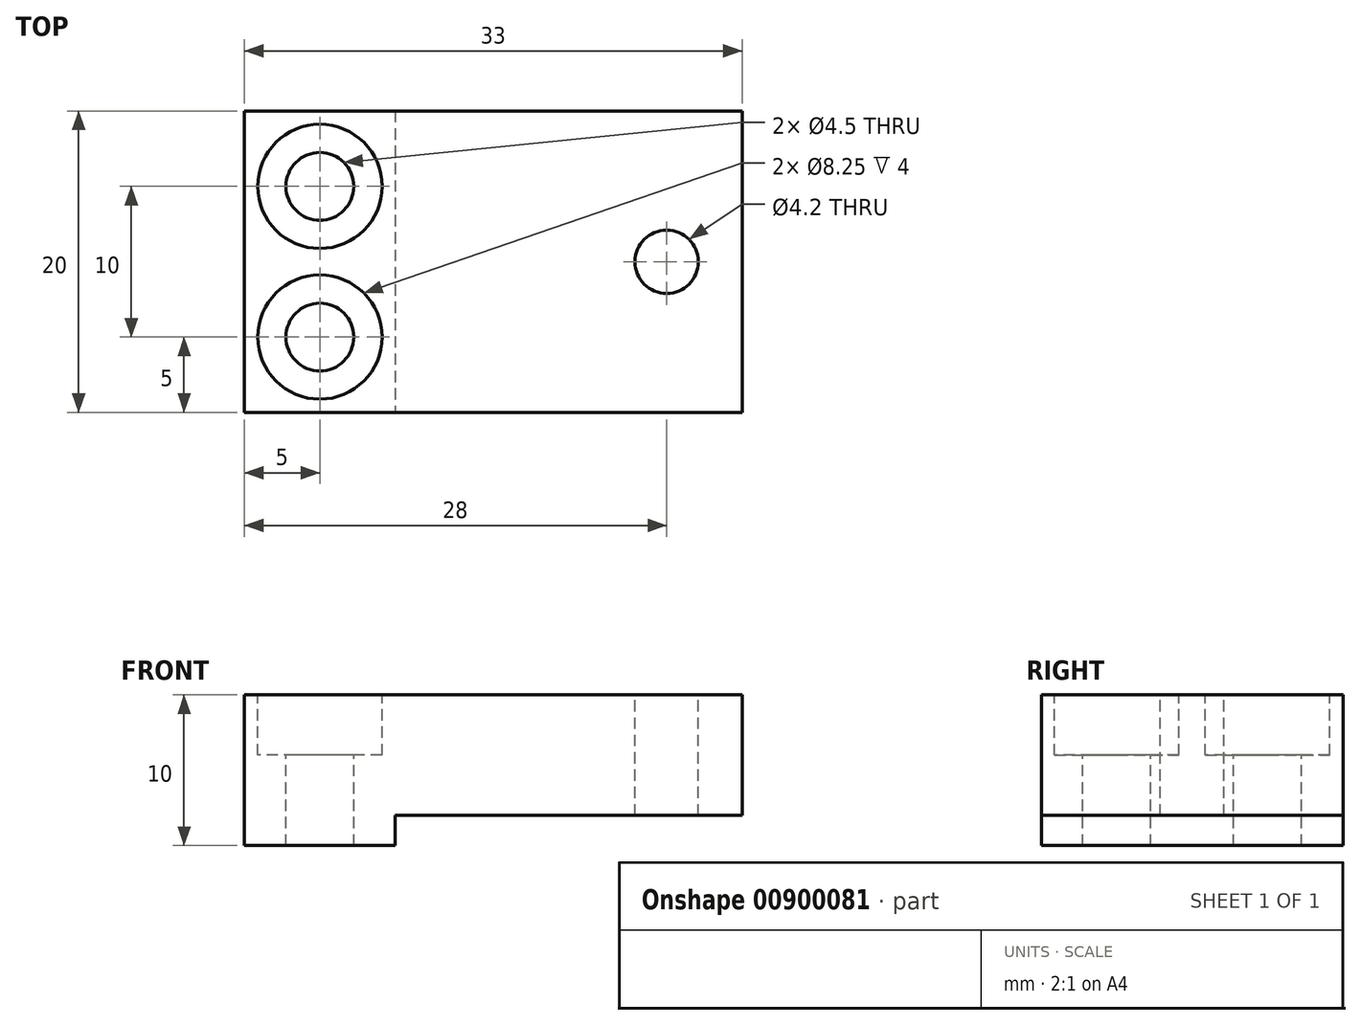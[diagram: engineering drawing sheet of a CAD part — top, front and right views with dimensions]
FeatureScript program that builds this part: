
annotation { "Feature Type Name" : "Feature", "Feature Type Description" : "" }
export const myFeature = defineFeature(function(context is Context, id is Id, definition is map)
    precondition{}
    {
        {
            var Q0;
            Q0=qCreatedBy(makeId("Top.planeOp"),FACE);
            var sketch = newSketch(context, id + "F0", { "sketchPlane" : qUnion([Q0])});
            skLineSegment(sketch, "E0.bottom", {"start": v(16.5, -10) * mm, "end": v(-16.5, -10) * mm});
            skLineSegment(sketch, "E0.top", {"start": v(16.5, 10) * mm, "end": v(-16.5, 10) * mm});
            skLineSegment(sketch, "E0.left", {"start": v(16.5, -10) * mm, "end": v(16.5, 10) * mm});
            skLineSegment(sketch, "E0.right", {"start": v(-16.5, -10) * mm, "end": v(-16.5, 10) * mm});
            skPoint(sketch, "E0.middle", {"position": v(0, 0) * mm});
            skLineSegment(sketch, "E1", {"start": v(-6.5, 10) * mm, "end": v(-6.5, -10) * mm});
            skLineSegment(sketch, "E2", {"start": v(-11.5, 5) * mm, "end": v(-11.5, -5) * mm, "construction": true});
            skLineSegment(sketch, "E3", {"start": v(0, 0) * mm, "end": v(11.5, 0) * mm, "construction": true});
            skSolve(sketch);
        }
        {
            var Q0;
            {var subQ0=sQuery(id+"F0.wireOp",EDGE,"E0.right");Q0=makeQuery(id+"F0.imprint","IMPRINT",FACE,{"disambiguationData":[TD([[makeQuery(id+"F0.imprint","IMPRINT",EDGE,{"derivedFrom":subQ0}),-1.0]])]});}
            extrude(context, id + "F1", {"entities" : qUnion([Q0]), "oppositeDirection" : true, "depth" : 10 * mm, "offsetDistance" : 25 * mm});
        }
        {
            var Q0;
            {var subQ0=sQuery(id+"F0.wireOp",EDGE,"E0.left");Q0=makeQuery(id+"F0.imprint","IMPRINT",FACE,{"disambiguationData":[TD([[makeQuery(id+"F0.imprint","IMPRINT",EDGE,{"derivedFrom":subQ0}),1.0]])]});}
            extrude(context, id + "F2", {"entities" : qUnion([Q0]), "operationType" : NewBodyOperationType.ADD, "oppositeDirection" : true, "depth" : 8 * mm, "offsetDistance" : 25 * mm});
        }
        {
            var Q0;
            Q0=sQuery(id+"F0.wireOp",VERTEX,"E3.end");
            var Q1;
            Q1=makeQuery(id+"F1.opExtrude","SWEPT_BODY",BODY,{"disambiguationData":[OSD([sQuery(id+"F0.wireOp",EDGE,"E0.bottom"),sQuery(id+"F0.wireOp",EDGE,"E0.top"),sQuery(id+"F0.wireOp",EDGE,"E0.right"),sQuery(id+"F0.wireOp",EDGE,"E1")])]});
            hole(context, id + "F3", {"style" : HoleStyle.SIMPLE, "endStyle" : HoleEndStyle.THROUGH, "standardTappedOrClearance" : lookupTablePath({ "standard" : "ISO", "engagement" : "75%", "pitch" : "0.8 mm", "size" : "M5", "type" : "Tapped" }), "standardBlindInLast" : lookupTablePath({ "standard" : "ISO", "engagement" : "75%", "pitch" : "0.8 mm", "size" : "M5", "type" : "Tapped" }), "holeDiameter" : 4.2 * mm, "majorDiameter" : 5 * mm, "showTappedDepth" : true, "tappedDepth" : 12 * mm, "tapClearance" : 3, "startFromSketch" : true, "locations" : qUnion([Q0]), "scope" : qUnion([Q1])});
        }
        {
            var Q0;
            Q0=sQuery(id+"F0.wireOp",VERTEX,"E2.start");
            var Q1;
            Q1=sQuery(id+"F0.wireOp",VERTEX,"E2.end");
            var Q2;
            Q2=makeQuery(id+"F1.opExtrude","SWEPT_BODY",BODY,{"disambiguationData":[OSD([sQuery(id+"F0.wireOp",EDGE,"E0.bottom"),sQuery(id+"F0.wireOp",EDGE,"E0.top"),sQuery(id+"F0.wireOp",EDGE,"E0.right"),sQuery(id+"F0.wireOp",EDGE,"E1")])]});
            hole(context, id + "F4", {"style" : HoleStyle.C_BORE, "endStyle" : HoleEndStyle.THROUGH, "standardTappedOrClearance" : lookupTablePath({ "fit" : "Normal", "standard" : "ISO", "size" : "M4", "type" : "Clearance" }), "standardBlindInLast" : lookupTablePath({ "fit" : "Normal", "standard" : "ISO", "size" : "M4", "type" : "Clearance" }), "holeDiameter" : 4.5 * mm, "cBoreDiameter" : 8.25 * mm, "cBoreDepth" : 4 * mm, "majorDiameter" : 4 * mm, "tappedDepth" : 12 * mm, "tapClearance" : 3, "startFromSketch" : true, "locations" : qUnion([Q0, Q1]), "scope" : qUnion([Q2])});
        }
    });
